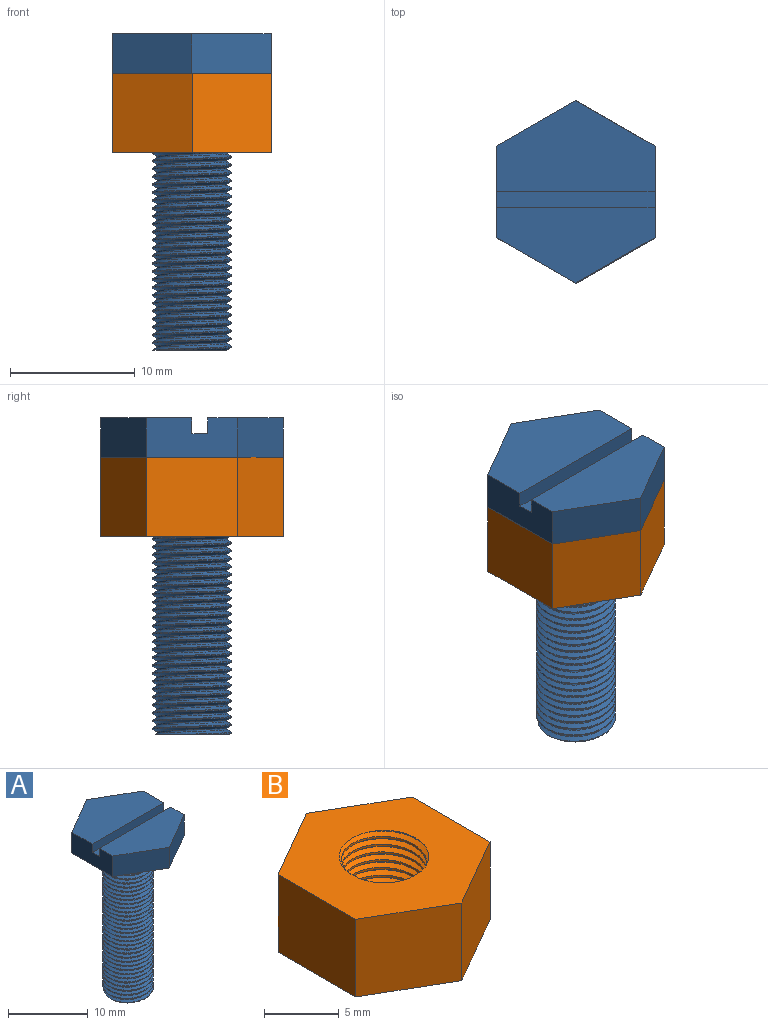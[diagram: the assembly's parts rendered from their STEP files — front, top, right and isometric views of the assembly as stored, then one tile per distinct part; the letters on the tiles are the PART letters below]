
ASSEMBLY  parts=2 mates=1
PART A: 17 faces, bbox 12.9x14.8x25.9 mm
  f0: plane 12.7x7.33mm, normal (0,0,1), area 69.8mm2, adj f7,f8,f9,f11,f14
  f1: cylinder r=3.17mm len=22.23mm, axis (0,0,-1), area 255.2mm2, adj f3,f4,f5,f6
  f2: bspline ~22.7x6.54mm, area 109.5mm2, adj f3,f4,f5,f6
  f3: bspline ~22.74x7.33mm, area 261.9mm2, adj f1,f2,f5,f6
  f4: bspline ~22.64x7.33mm, area 263.1mm2, adj f1,f2,f5,f6
  f5: plane 6.16x6.13mm, normal (0,0,-1), area 27.9mm2, adj f1,f2,f3,f4
  f6: plane 14.85x12.89mm, normal (0,0,-1), area 111.8mm2, adj f1,f2,f3,f4,f7,f8,f9,f10
  f7: plane 7.33x3.18mm, normal (1,0,0), area 21.7mm2, adj f0,f6,f8,f10,f13,f14,f15,f16
  f8: plane 6.35x3.67mm, normal (0.5,0.87,0), area 23.3mm2, adj f0,f6,f7,f9
  f9: plane 6.35x3.67mm, normal (-0.5,0.87,0), area 23.3mm2, adj f0,f6,f8,f11
  f10: plane 6.35x3.67mm, normal (0.5,-0.87,0), area 23.3mm2, adj f6,f7,f12,f13
  f11: plane 7.33x3.18mm, normal (-1,0,0), area 21.7mm2, adj f0,f6,f9,f12,f13,f14,f15,f16
  f12: plane 6.35x3.67mm, normal (-0.5,-0.87,0), area 23.3mm2, adj f6,f10,f11,f13
  f13: plane 12.7x6.06mm, normal (0,0,1), area 53.7mm2, adj f7,f10,f11,f12,f15
  f14: plane 12.7x1.27mm, normal (0,-1,0), area 16.1mm2, adj f0,f7,f11,f16
  f15: plane 12.7x1.27mm, normal (0,1,0), area 16.1mm2, adj f7,f11,f13,f16
  f16: plane 12.7x1.27mm, normal (0,0,1), area 16.1mm2, adj f7,f11,f14,f15
PART B: 12 faces, bbox 12.9x14.9x7.1 mm
  f0: plane 6.35x6.35mm, normal (0.5,-0.87,0), area 46.6mm2, adj f1,f5,f6,f7
  f1: plane 7.33x6.35mm, normal (1,0,0), area 46.6mm2, adj f0,f2,f6,f7
  f2: plane 6.35x6.35mm, normal (0.5,0.87,0), area 46.6mm2, adj f1,f3,f6,f7
  f3: plane 6.35x6.35mm, normal (-0.5,0.87,0), area 46.6mm2, adj f2,f4,f6,f7
  f4: plane 7.33x6.35mm, normal (-1,0,0), area 46.6mm2, adj f3,f5,f6,f7
  f5: plane 6.35x6.35mm, normal (-0.5,-0.87,0), area 46.6mm2, adj f0,f4,f6,f7
  f6: plane 14.86x12.89mm, normal (0,0,1), area 111.2mm2, adj f0,f1,f2,f3,f4,f5,f8,f9
  f7: plane 14.86x12.89mm, normal (0,0,-1), area 111.2mm2, adj f0,f1,f2,f3,f4,f5,f8,f9
  f8: bspline ~7.39x6.76mm, area 75.4mm2, adj f6,f7,f10,f11
  f9: bspline ~7.39x6.87mm, area 75.6mm2, adj f6,f7,f10,f11
  f10: bspline ~7.46x6.64mm, area 18.6mm2, adj f6,f7,f8,f9
  f11: cylinder r=2.86mm len=6.35mm, axis (0,0,1), area 30.9mm2, adj f6,f7,f8,f9
PLACE A at identity fixed
PLACE B rot(axis=(0,0,-1),180deg) t=(0.01,-0.02,15.88)mm
MATE cylindrical A.f6 <-> B.f6  axis (0,0,-1) through (0.04,0.02,22.22)mm
